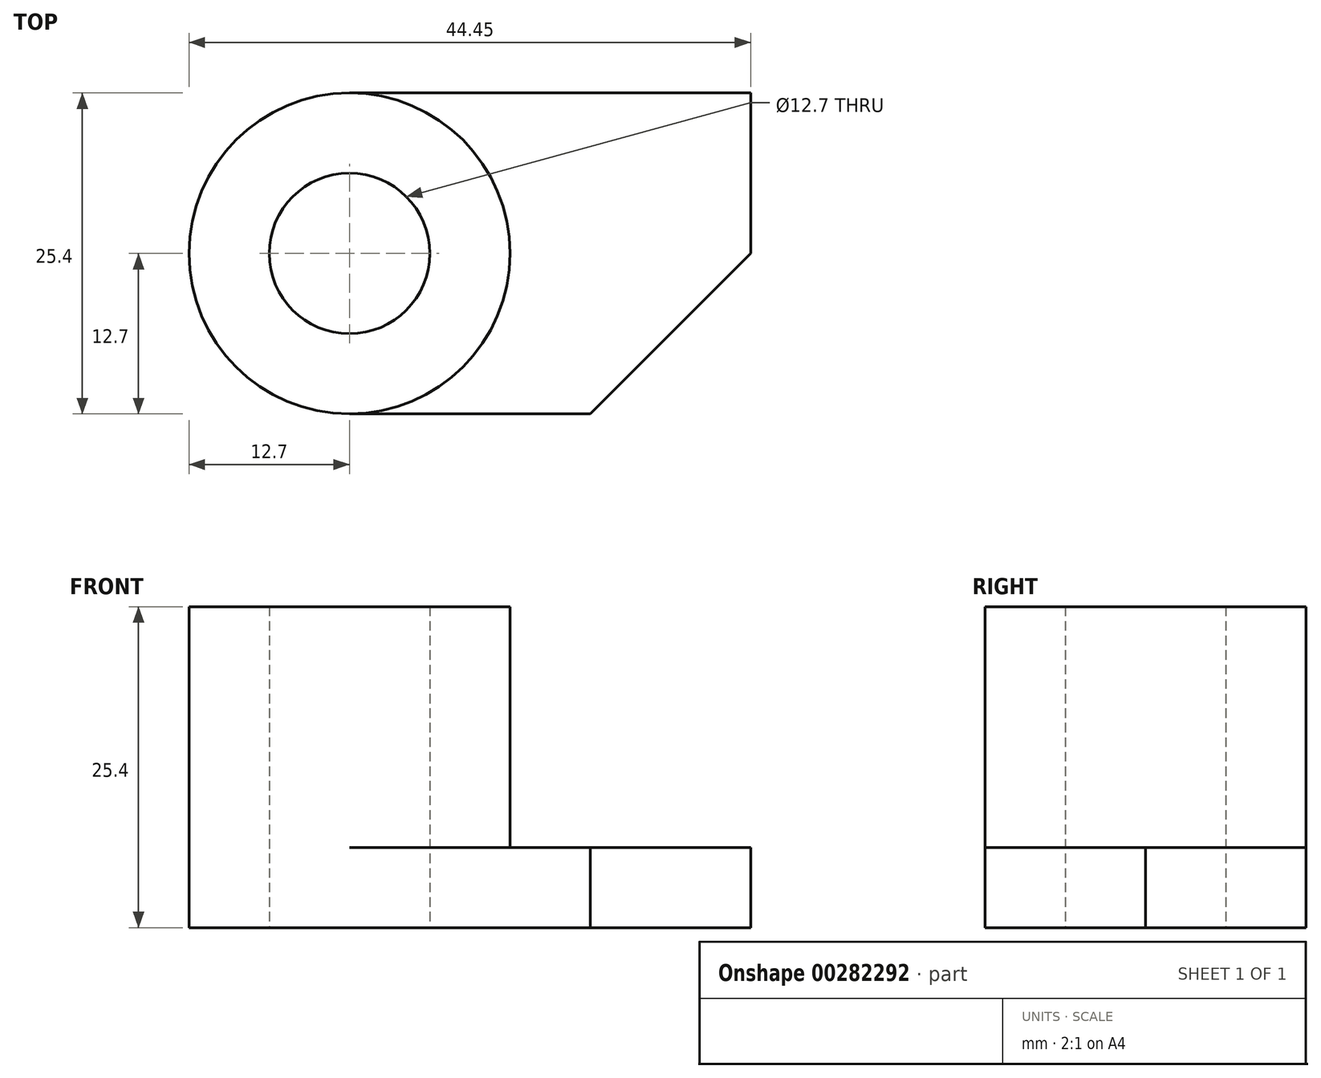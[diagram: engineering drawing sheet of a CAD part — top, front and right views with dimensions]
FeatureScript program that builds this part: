
annotation { "Feature Type Name" : "Feature", "Feature Type Description" : "" }
export const myFeature = defineFeature(function(context is Context, id is Id, definition is map)
    precondition{}
    {
        {
            var Q0;
            Q0=qCreatedBy(makeId("Top.planeOp"),FACE);
            var sketch = newSketch(context, id + "F0", { "sketchPlane" : qUnion([Q0])});
            skLineSegment(sketch, "E0", {"start": v(0, 0) * mm, "end": v(31.75, 0) * mm});
            skLineSegment(sketch, "E1", {"start": v(31.75, 0) * mm, "end": v(31.75, -12.7) * mm});
            skLineSegment(sketch, "E2", {"start": v(31.75, -12.7) * mm, "end": v(19.05, -25.4) * mm});
            skLineSegment(sketch, "E3", {"start": v(19.05, -25.4) * mm, "end": v(0, -25.4) * mm});
            skArc(sketch, "E4", {"start": v(0, 0) * mm, "mid": v(-12.7, -12.7) * mm, "end": v(0, -25.4) * mm});
            skCircle(sketch, "E5", {"center": v(0, -12.7) * mm, "radius": 6.35 * mm});
            skSolve(sketch);
        }
        {
            var Q0;
            Q0 = qSketchRegion(id + "F0", true);
            extrude(context, id + "F1", {"entities" : qUnion([Q0]), "depth" : 6.35 * mm});
        }
        {
            var Q0;
            Q0=makeQuery(id+"F1.opExtrude","CAP_FACE",FACE,{"disambiguationData":[OSD([sQuery(id+"F0.wireOp",EDGE,"E0"),sQuery(id+"F0.wireOp",EDGE,"E1"),sQuery(id+"F0.wireOp",EDGE,"E2"),sQuery(id+"F0.wireOp",EDGE,"E3"),sQuery(id+"F0.wireOp",EDGE,"E4")])],"isStart":false});
            var sketch = newSketch(context, id + "F2", { "sketchPlane" : qUnion([Q0])});
            skCircle(sketch, "E6", {"center": v(0, -12.7) * mm, "radius": 12.7 * mm});
            skCircle(sketch, "E7", {"center": v(0, -12.7) * mm, "radius": 6.35 * mm});
            skSolve(sketch);
        }
        {
            var Q0;
            Q0 = qSketchRegion(id + "F2", true);
            extrude(context, id + "F3", {"entities" : qUnion([Q0]), "operationType" : NewBodyOperationType.ADD, "depth" : 19.05 * mm});
        }
    });
